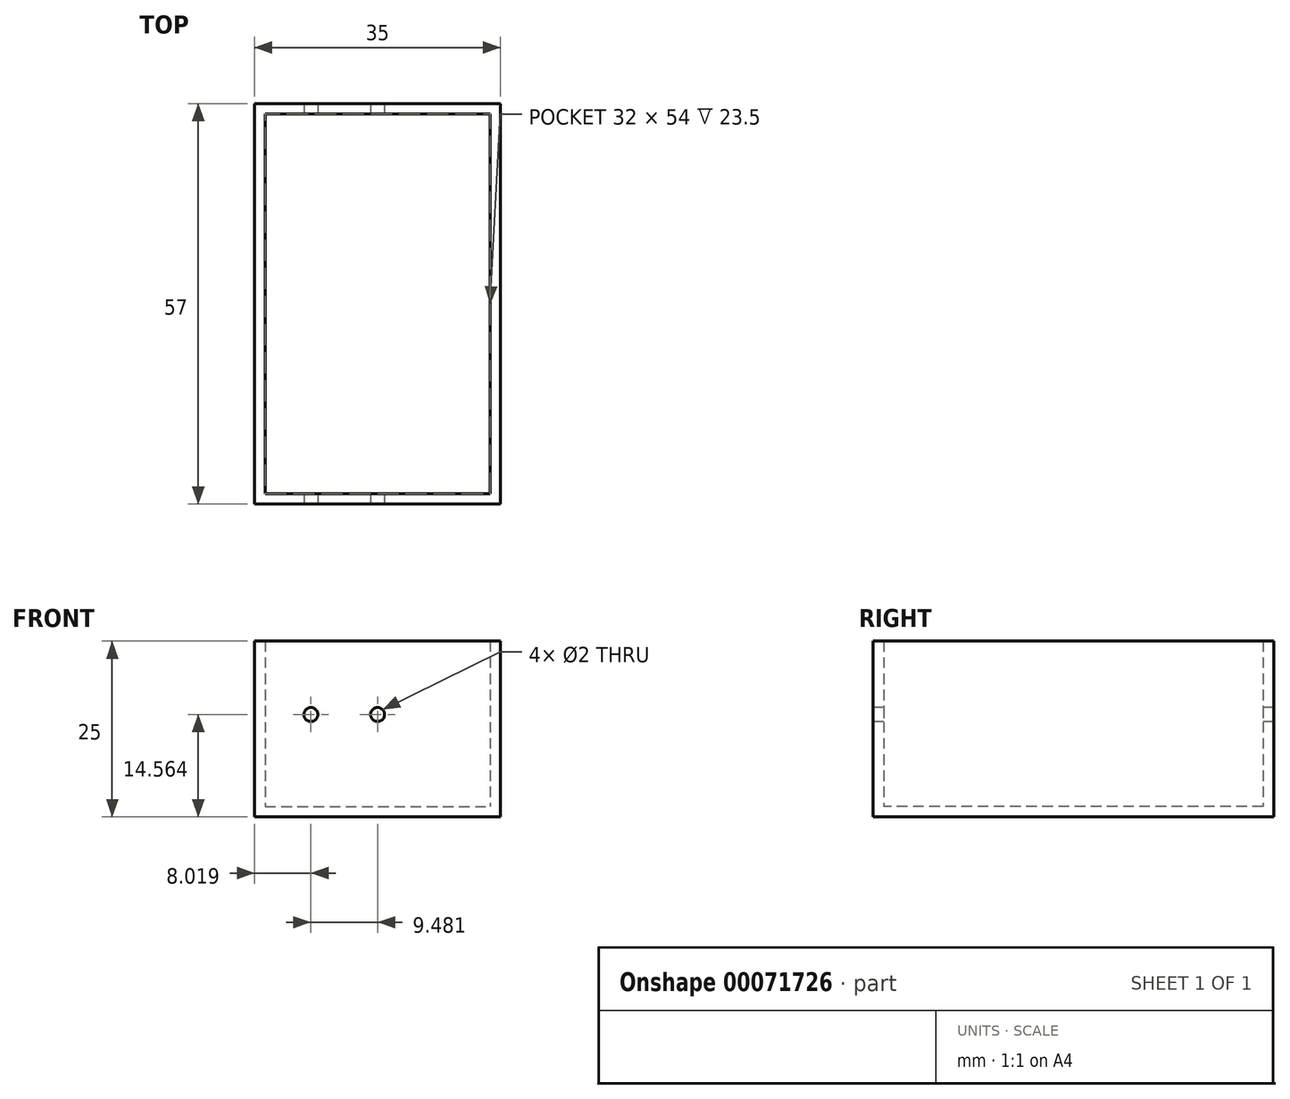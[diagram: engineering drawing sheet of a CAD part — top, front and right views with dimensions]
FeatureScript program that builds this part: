
annotation { "Feature Type Name" : "Feature", "Feature Type Description" : "" }
export const myFeature = defineFeature(function(context is Context, id is Id, definition is map)
    precondition{}
    {
        {
            var Q0;
            Q0=qCreatedBy(makeId("Top.planeOp"),FACE);
            var sketch = newSketch(context, id + "F0", { "sketchPlane" : qUnion([Q0])});
            skLineSegment(sketch, "E0.rect.bottom", {"start": v(-17.5, 28.5) * mm, "end": v(17.5, 28.5) * mm});
            skLineSegment(sketch, "E0.rect.top", {"start": v(-17.5, -28.5) * mm, "end": v(17.5, -28.5) * mm});
            skLineSegment(sketch, "E0.rect.left", {"start": v(-17.5, 28.5) * mm, "end": v(-17.5, -28.5) * mm});
            skLineSegment(sketch, "E0.rect.right", {"start": v(17.5, 28.5) * mm, "end": v(17.5, -28.5) * mm});
            skPoint(sketch, "E0.rect.middle", {"position": v(0, 0) * mm});
            skSolve(sketch);
        }
        {
            var Q0;
            Q0=makeQuery(id+"F0.imprint","IMPRINT",FACE,{"disambiguationData":[TD([[makeQuery(id+"F0.imprint","IMPRINT",EDGE,{"derivedFrom":sQuery(id+"F0.wireOp",EDGE,"E0.rect.bottom")}),-1.0]])]});
            extrude(context, id + "F1", {"entities" : qUnion([Q0]), "depth" : 25 * mm});
        }
        {
            var Q0;
            Q0=makeQuery(id+"F1.opExtrude","CAP_FACE",FACE,{"disambiguationData":[OSD([sQuery(id+"F0.wireOp",EDGE,"E0.rect.bottom"),sQuery(id+"F0.wireOp",EDGE,"E0.rect.top"),sQuery(id+"F0.wireOp",EDGE,"E0.rect.left"),sQuery(id+"F0.wireOp",EDGE,"E0.rect.right")])],"isStart":false});
            shell(context, id + "F2", {"entities" : qUnion([Q0]), "thickness" : 1.5 * mm});
        }
        {
            var Q0;
            Q0=makeQuery(id+"F1.opExtrude","SWEPT_FACE",FACE,{"disambiguationData":[OSD([sQuery(id+"F0.wireOp",EDGE,"E0.rect.top")])]});
            var sketch = newSketch(context, id + "F3", { "sketchPlane" : qUnion([Q0])});
            skCircle(sketch, "E1", {"center": v(0, 14.56) * mm, "radius": 2.23 * mm});
            skCircle(sketch, "E2", {"center": v(-9.48, 14.56) * mm, "radius": 2.3 * mm});
            skSolve(sketch);
        }
        {
            var Q0;
            Q0=sQuery(id+"F3.wireOp",VERTEX,"E2.center");
            var Q1;
            Q1=sQuery(id+"F3.wireOp",VERTEX,"E1.center");
            var Q2;
            Q2=makeQuery(id+"F1.opExtrude","SWEPT_BODY",BODY,{"disambiguationData":[OSD([sQuery(id+"F0.wireOp",EDGE,"E0.rect.bottom"),sQuery(id+"F0.wireOp",EDGE,"E0.rect.top"),sQuery(id+"F0.wireOp",EDGE,"E0.rect.left"),sQuery(id+"F0.wireOp",EDGE,"E0.rect.right")])]});
            hole(context, id + "F4", {"style" : HoleStyle.SIMPLE, "holeDiameter" : 2 * mm, "endStyle" : HoleEndStyle.THROUGH, "locations" : qUnion([Q0, Q1]), "scope" : qUnion([Q2])});
        }
    });
